# Revit family: Partition-6_Panels_High-Skyfold_Classic_Zenith-10-1_to_12-0_FC_3075_to_3660
name_source: partatom
category: Generic Models
units: mm (PartAtom-declared; Revit-internal decimal feet)

## family parameters
Always vertical = Yes
Can host rebar = No
Cut with Voids When Loaded = No
Host = Ceiling
Maintain Annotation Orientation = No
Part Type = Normal
Room Calculation Point = No
Round Connector Dimension = Use Diameter
Shared = No

## types (5) — shared parameters
Default Elevation = 0' - 0"
Distance From Acoustic Barrier = 0' - 2"
Model = Compact Drive System
URL = http://www.skyfold.com
Wall Thickness = 0' - 11 3/4"

## per-type parameters (varying)
| type | Acoustic Barrier"C" | Beam Height"B" | Description | Finished Ceiling"A" | Manufacturer | Panel Height"F" | Pocket Depth"D" | Pocket Width"E" | Total Panel Height |
| 10'- 1" | 11' - 9 1/4" | 12' - 9" | Custom Powerlift Partitions | 10' - 1" | Skyfold | 1' - 10 5/8" | 1' - 8 1/4" | 4' - 7" | 11' - 6 1/4" |
| 11' - 0" | 12' - 8 1/2" | 13' - 8 1/4" | Custom Powerlift Partitions | 11' - 0" | Skyfold | 2' - 0 1/2" | 1' - 8 1/2" | 4' - 10 3/4" | 12' - 5 1/2" |
| 10' - 6" | 12' - 2 1/2" | 13' - 2 1/4" | Custom Powerlift Partitions | 10' - 6" | Skyfold | 1' - 11 1/2" | 1' - 8 1/2" | 4' - 8 3/4" | 11' - 11 1/2" |
| 11' - 6" | 13' - 2 1/2" | 14' - 2 1/4" | Custom Powerlift Partitions
Custom Powerlift Partitions | 11' - 6" | Skyfold | 2' - 1 1/2" | 1' - 8 1/2" | 5' - 0 3/4" | 12' - 11 1/2" |
| 12' - 0" | 13' - 8 1/2" | 14' - 8 1/4" | Custom Powerlift Partitions | 12' - 0" | Skyfold
Skyfold | 2' - 2 1/2" | 1' - 8 1/2" | 5' - 2 3/4" | 13' - 5 1/2" |

## geometry (parser evidence)
native form markers: Sweep x25
no freeform markers — native parametric forms only
